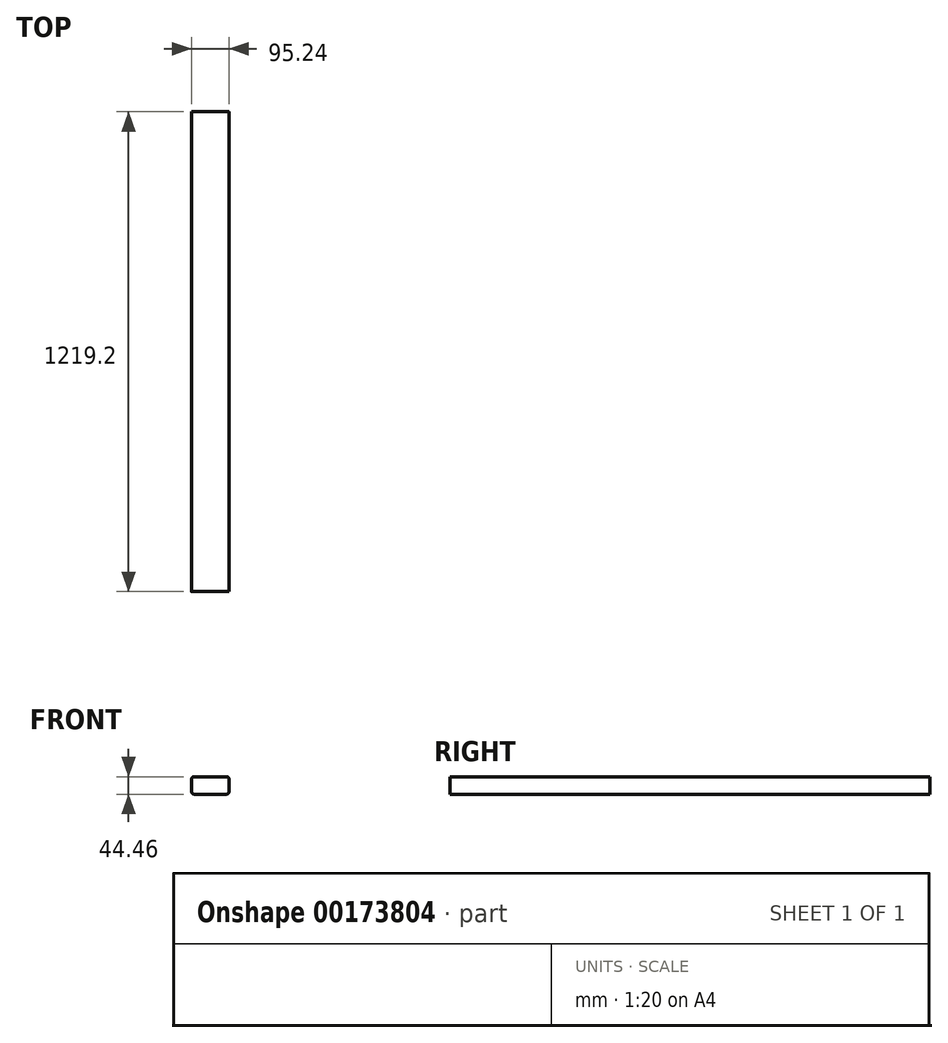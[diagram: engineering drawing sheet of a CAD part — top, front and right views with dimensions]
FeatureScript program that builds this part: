
annotation { "Feature Type Name" : "Feature", "Feature Type Description" : "" }
export const myFeature = defineFeature(function(context is Context, id is Id, definition is map)
    precondition{}
    {
        {
            var Q0;
            Q0=qCreatedBy(makeId("Front.planeOp"),FACE);
            var sketch = newSketch(context, id + "F0", { "sketchPlane" : qUnion([Q0])});
            skLineSegment(sketch, "E0.bottom", {"start": v(41.28, 22.23) * mm, "end": v(-41.27, 22.23) * mm});
            skLineSegment(sketch, "E0.top", {"start": v(41.28, -22.23) * mm, "end": v(-41.27, -22.23) * mm});
            skLineSegment(sketch, "E0.left", {"start": v(47.63, 15.88) * mm, "end": v(47.63, -15.88) * mm});
            skLineSegment(sketch, "E0.right", {"start": v(-47.63, 15.88) * mm, "end": v(-47.63, -15.88) * mm});
            skPoint(sketch, "E0.middle", {"position": v(0, 0) * mm});
            skPoint(sketch, "E1.visualSharp", {"position": v(-47.63, 22.23) * mm});
            skArc(sketch, "E1.filletArc", {"start": v(-41.27, 22.23) * mm, "mid": v(-45.77, 20.37) * mm, "end": v(-47.62, 15.88) * mm});
            skPoint(sketch, "E2.visualSharp", {"position": v(47.63, 22.23) * mm});
            skArc(sketch, "E2.filletArc", {"start": v(47.63, 15.88) * mm, "mid": v(45.77, 20.37) * mm, "end": v(41.28, 22.23) * mm});
            skPoint(sketch, "E3.visualSharp", {"position": v(47.63, -22.23) * mm});
            skArc(sketch, "E3.filletArc", {"start": v(41.28, -22.23) * mm, "mid": v(45.77, -20.37) * mm, "end": v(47.63, -15.88) * mm});
            skPoint(sketch, "E4.visualSharp", {"position": v(-47.63, -22.23) * mm});
            skArc(sketch, "E4.filletArc", {"start": v(-47.62, -15.88) * mm, "mid": v(-45.77, -20.37) * mm, "end": v(-41.27, -22.23) * mm});
            skSolve(sketch);
        }
        {
            var Q0;
            Q0 = qSketchRegion(id + "F0", true);
            extrude(context, id + "F1", {"entities" : qUnion([Q0]), "depth" : 1219.2 * mm});
        }
    });
